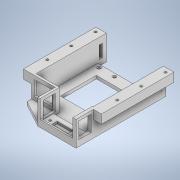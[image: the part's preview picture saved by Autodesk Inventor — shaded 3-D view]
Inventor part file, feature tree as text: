
AUTODESK INVENTOR PART (.ipt)
format: ipt  version: 2021.1 (Build 251245010, 245A)  size: 451,072 bytes
history: native  units: mm
features: extrude x21, sketch x17, other x9, projected_geometry x7, reference x6, revolve x2, mirror x1
ambient origin geometry x8: Origin, YZ Plane, XZ Plane, XY Plane, X Axis, Y Axis, Z Axis, Center Point
bodies: Body1 (feature_tree)
feature tree (63):
  other  "Твердое тело1"
  extrude  "Выдавливание1"  Depth=84.0mm
  extrude  "Выдавливание2"  Depth=22.0mm
  extrude  "Выдавливание3"  Depth=11.0mm
  sketch  "Эскиз4"
  extrude  "Выдавливание4"  Depth=12.0mm
  extrude  "Выдавливание5"  Depth=106.0mm
  extrude  "Выдавливание6"  Depth=122.0mm TaperAngle=0.0deg
  extrude  "Выдавливание7"  Depth=4.2mm
  extrude  "Выдавливание8"  Depth=14.25mm
  extrude  "Выдавливание9"  Depth=14.25mm
  extrude  "Выдавливание10"  Depth=95.5mm TaperAngle=0.0deg
  extrude  "Выдавливание11"  Depth=1.0mm
  sketch  "Эскиз7"
  extrude  "Выдавливание12"  Depth=44.54mm
  extrude  "Выдавливание13"  Depth=8.25mm TaperAngle=0.0deg
  extrude  "Выдавливание14"  Depth=35.5mm
  extrude  "Выдавливание15"  Depth=9.0mm
  extrude  "Выдавливание16"  Depth=3.0mm
  sketch  "Эскиз11"
  extrude  "Выдавливание17"  Depth=3.0mm
  extrude  "Выдавливание18"  Depth=4.25mm
  extrude  "Выдавливание19"  Depth=1.75mm
  other  "РабПлоскость1"
  sketch  "Эскиз14"
  sketch  "Эскиз15"
  extrude  "Выдавливание20"  Depth=26.8mm TaperAngle=0.0deg
  extrude  "Выдавливание21"  Depth=35.3mm TaperAngle=0.0deg
  sketch  "Эскиз16"
  other  "РабПлоскость2"
  other  "РабПлоскость3"
  other  "РабПлоскость4"
  revolve  "Вращение1"
  revolve  "Вращение2"
  mirror  "Зеркальное отражение1"
  sketch  "Эскиз1"
  sketch  "Эскиз2"
  projected_geometry  "Спроецированная петля1"
  sketch  "Эскиз3"
  projected_geometry  "Спроецированная петля2"
  projected_geometry  "Спроецированная петля3"
  sketch  "Эскиз5"
  sketch  "Эскиз6"
  projected_geometry  "Спроецированная петля4"
  sketch  "Эскиз8"
  projected_geometry  "Спроецированная петля5"
  sketch  "Эскиз9"
  projected_geometry  "Спроецированная петля6"
  sketch  "Эскиз10"
  reference  "Ссылка1"
  reference  "Ссылка2"
  projected_geometry  "Спроецированная петля7"
  sketch  "Эскиз12"
  reference  "Ссылка3"
  reference  "Ссылка4"
  reference  "Ссылка5"
  reference  "Ссылка6"
  sketch  "Эскиз17"
  sketch  "Эскиз18"
  other  "<userpath>\Documents\новая сборка для аккумулятора\сборка корпуса для аккумулятора 3.iam"
  other  "сборка корпуса для аккумулятора 3.iam"
  other  "плата переходник:1"
  other  "средняя часть дверцы:1"
